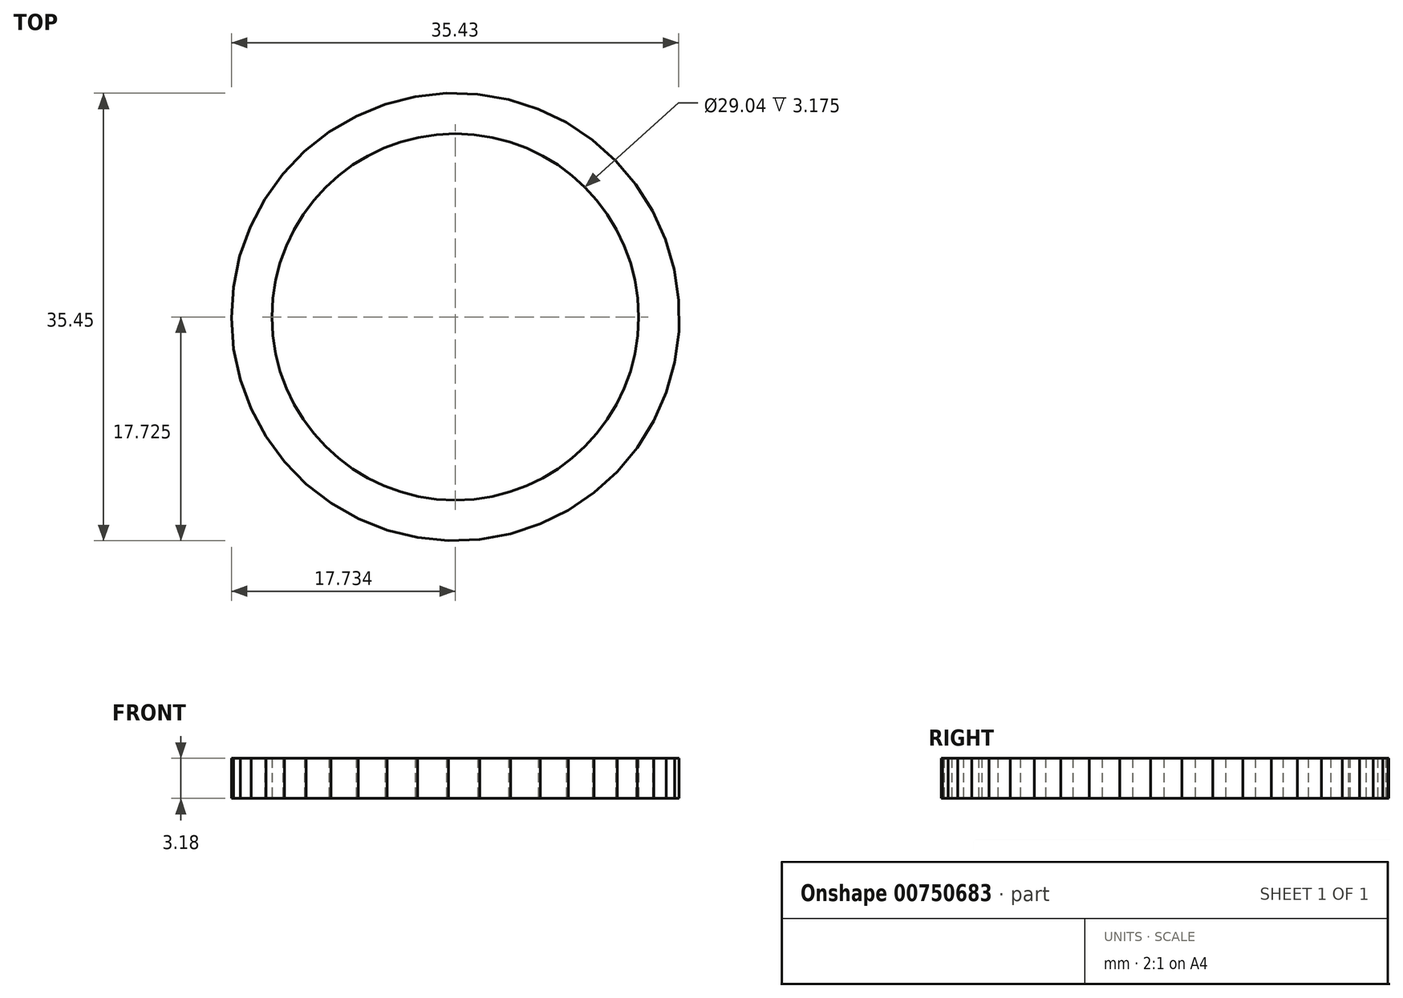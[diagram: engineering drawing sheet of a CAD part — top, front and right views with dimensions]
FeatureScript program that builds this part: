
annotation { "Feature Type Name" : "Feature", "Feature Type Description" : "" }
export const myFeature = defineFeature(function(context is Context, id is Id, definition is map)
    precondition{}
    {
        {
            var Q0;
            Q0=qCreatedBy(makeId("Top.planeOp"),FACE);
            var sketch = newSketch(context, id + "F0", { "sketchPlane" : qUnion([Q0])});
            skLineSegment(sketch, "E0", {"start": v(-103.18, 7.52) * mm, "end": v(-100.08, 11) * mm});
            skLineSegment(sketch, "E1", {"start": v(-100.08, 11) * mm, "end": v(-98.87, 6.36) * mm});
            skCircle(sketch, "E2.cCircle", {"center": v(-102.24, 36.4) * mm, "radius": 17.74 * mm, "construction": true});
            skLineSegment(sketch, "E2.0", {"start": v(-105.23, 18.91) * mm, "end": v(-107.63, 19.5) * mm});
            skLineSegment(sketch, "E2.1", {"start": v(-107.63, 19.5) * mm, "end": v(-109.93, 20.42) * mm});
            skLineSegment(sketch, "E2.2", {"start": v(-109.93, 20.42) * mm, "end": v(-112.08, 21.64) * mm});
            skLineSegment(sketch, "E2.3", {"start": v(-112.08, 21.64) * mm, "end": v(-114.04, 23.16) * mm});
            skLineSegment(sketch, "E2.4", {"start": v(-114.04, 23.16) * mm, "end": v(-115.76, 24.93) * mm});
            skLineSegment(sketch, "E2.5", {"start": v(-115.76, 24.93) * mm, "end": v(-117.23, 26.92) * mm});
            skLineSegment(sketch, "E2.6", {"start": v(-117.23, 26.92) * mm, "end": v(-118.4, 29.1) * mm});
            skLineSegment(sketch, "E2.7", {"start": v(-118.4, 29.1) * mm, "end": v(-119.26, 31.42) * mm});
            skLineSegment(sketch, "E2.8", {"start": v(-119.26, 31.42) * mm, "end": v(-119.79, 33.84) * mm});
            skLineSegment(sketch, "E2.9", {"start": v(-119.79, 33.84) * mm, "end": v(-119.97, 36.3) * mm});
            skLineSegment(sketch, "E2.10", {"start": v(-119.97, 36.3) * mm, "end": v(-119.81, 38.78) * mm});
            skLineSegment(sketch, "E2.11", {"start": v(-119.81, 38.78) * mm, "end": v(-119.3, 41.2) * mm});
            skLineSegment(sketch, "E2.12", {"start": v(-119.3, 41.2) * mm, "end": v(-118.47, 43.53) * mm});
            skLineSegment(sketch, "E2.13", {"start": v(-118.47, 43.53) * mm, "end": v(-117.32, 45.72) * mm});
            skLineSegment(sketch, "E2.14", {"start": v(-117.32, 45.72) * mm, "end": v(-115.88, 47.73) * mm});
            skLineSegment(sketch, "E2.15", {"start": v(-115.88, 47.73) * mm, "end": v(-114.17, 49.52) * mm});
            skLineSegment(sketch, "E2.16", {"start": v(-114.17, 49.52) * mm, "end": v(-112.23, 51.05) * mm});
            skLineSegment(sketch, "E2.17", {"start": v(-112.23, 51.05) * mm, "end": v(-110.1, 52.3) * mm});
            skLineSegment(sketch, "E2.18", {"start": v(-110.1, 52.3) * mm, "end": v(-107.8, 53.24) * mm});
            skLineSegment(sketch, "E2.19", {"start": v(-107.8, 53.24) * mm, "end": v(-105.4, 53.85) * mm});
            skLineSegment(sketch, "E2.20", {"start": v(-105.4, 53.85) * mm, "end": v(-102.94, 54.12) * mm});
            skLineSegment(sketch, "E2.21", {"start": v(-102.94, 54.12) * mm, "end": v(-100.47, 54.04) * mm});
            skLineSegment(sketch, "E2.22", {"start": v(-100.47, 54.04) * mm, "end": v(-98.03, 53.63) * mm});
            skLineSegment(sketch, "E2.23", {"start": v(-98.03, 53.63) * mm, "end": v(-95.67, 52.87) * mm});
            skLineSegment(sketch, "E2.24", {"start": v(-95.67, 52.87) * mm, "end": v(-93.44, 51.8) * mm});
            skLineSegment(sketch, "E2.25", {"start": v(-93.44, 51.8) * mm, "end": v(-91.39, 50.43) * mm});
            skLineSegment(sketch, "E2.26", {"start": v(-91.39, 50.43) * mm, "end": v(-89.54, 48.78) * mm});
            skLineSegment(sketch, "E2.27", {"start": v(-89.54, 48.78) * mm, "end": v(-87.94, 46.9) * mm});
            skLineSegment(sketch, "E2.28", {"start": v(-87.94, 46.9) * mm, "end": v(-86.62, 44.8) * mm});
            skLineSegment(sketch, "E2.29", {"start": v(-86.62, 44.8) * mm, "end": v(-85.6, 42.54) * mm});
            skLineSegment(sketch, "E2.30", {"start": v(-85.6, 42.54) * mm, "end": v(-84.9, 40.17) * mm});
            skLineSegment(sketch, "E2.31", {"start": v(-84.9, 40.17) * mm, "end": v(-84.55, 37.72) * mm});
            skLineSegment(sketch, "E2.32", {"start": v(-84.55, 37.72) * mm, "end": v(-84.54, 35.25) * mm});
            skLineSegment(sketch, "E2.33", {"start": v(-84.54, 35.25) * mm, "end": v(-84.87, 32.8) * mm});
            skLineSegment(sketch, "E2.34", {"start": v(-84.87, 32.8) * mm, "end": v(-85.54, 30.41) * mm});
            skLineSegment(sketch, "E2.35", {"start": v(-85.54, 30.41) * mm, "end": v(-86.53, 28.15) * mm});
            skLineSegment(sketch, "E2.36", {"start": v(-86.53, 28.15) * mm, "end": v(-87.84, 26.04) * mm});
            skLineSegment(sketch, "E2.37", {"start": v(-87.84, 26.04) * mm, "end": v(-89.42, 24.14) * mm});
            skLineSegment(sketch, "E2.38", {"start": v(-89.42, 24.14) * mm, "end": v(-91.25, 22.47) * mm});
            skLineSegment(sketch, "E2.39", {"start": v(-91.25, 22.47) * mm, "end": v(-93.3, 21.08) * mm});
            skLineSegment(sketch, "E2.40", {"start": v(-93.3, 21.08) * mm, "end": v(-95.5, 19.99) * mm});
            skLineSegment(sketch, "E2.41", {"start": v(-95.5, 19.99) * mm, "end": v(-97.86, 19.2) * mm});
            skLineSegment(sketch, "E2.42", {"start": v(-97.86, 19.2) * mm, "end": v(-100.3, 18.77) * mm});
            skLineSegment(sketch, "E2.43", {"start": v(-100.3, 18.77) * mm, "end": v(-102.77, 18.67) * mm});
            skLineSegment(sketch, "E2.44", {"start": v(-102.77, 18.67) * mm, "end": v(-105.23, 18.91) * mm});
            skCircle(sketch, "E3", {"center": v(-102.24, 36.4) * mm, "radius": 14.52 * mm});
            skSolve(sketch);
        }
        {
            var Q0;
            Q0=makeQuery(id+"F0.imprint","IMPRINT",FACE,{"disambiguationData":[TD([[makeQuery(id+"F0.imprint","IMPRINT",EDGE,{"derivedFrom":sQuery(id+"F0.wireOp",EDGE,"E2.0")}),-1.0]])]});
            extrude(context, id + "F1", {"entities" : qUnion([Q0]), "depth" : 3.17 * mm, "offsetDistance" : 25.4 * mm});
        }
    });
